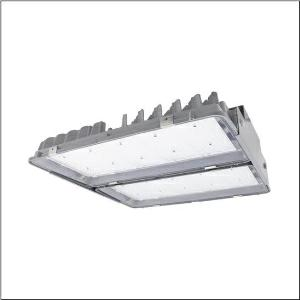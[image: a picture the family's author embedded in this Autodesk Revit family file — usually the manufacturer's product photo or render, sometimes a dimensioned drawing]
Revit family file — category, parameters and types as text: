
# Revit family: highbay_11xtreme_51hf81db4vma
name_source: partatom
category: Lighting Fixtures
units: mm (PartAtom-declared; Revit-internal decimal feet)

## family parameters
Cut with Voids When Loaded = No
Host = Face
Light Source = No
Part Type = Normal
Room Calculation Point = No
Round Connector Dimension = Use Diameter
Shared = No

## types (1)
- --- (1 x LED, 69400 lm, 380.2 W, 4000K)
    Apparent Load = 380 VA
    CIE Flux Codes = 88 96 99 100 100
    Color Rendering = 80
    Color Temperature = 4000K
    Default Elevation = 1800 mm
    Description = Highbay 11Xtreme, LED high bay luminaire, primary light control with lens, of PMMA, primary optical cover: cover, of toughened safety glass, light emission: direct distribution, primary light characteristic: symmetric, installation type: suspended mounting, surface-mounted, 2x LED module,for 1x 2x LED, rated luminous flux: 69.400lm, luminous efficacy: 183lm/W, light colour: 840, colour temperature: 4000K, with cable H07RN-F 5x 1.5mm², mains connection: 220..240V, AC, 50/60Hz, cable length: 1,5m, rated input power: 380W, luminaire housing, of diecast aluminium, partly coated, silver, length: 595mm, width: 560mm, height: 195mm, protection rating (complete): IP66, insulation class (complete): insulation class I (protective earthing), certification: CE, ENEC, UKCA, protection symbol: D, ball protection: ball impact resistant according to DIN VDE 0710 part 13 (with chain suspension), impact resistance: IK08, permissible operating ambient temperature: -25..+45°C, reducing of maximum allowable ambient temperature of 5°C with ceiling mounting, packaging unit: 1 piece
    Height = 157 mm
    Lamp = 1 x LED
    Lamp Light Flux = 69400 lm
    Lamp Power = 380.2 W
    Lamp count = 1
    Length = 593 mm
    Luminous efficacy = 183 lm/W
    Manufacturer = Siteco
    ModVariant = No
    Model = 51HF81DB4VMA
    Mounting Place = Ceiling
    Mounting Type = Pendant
    Number of Poles = 1
    OnlyDefault = Yes
    Power Factor = 1
    Product Name = Highbay 11Xtreme
    Product group = LED high bay luminaire
    ProductGroupID = 903
    Protection Class = Protection class I
    Protection Degree = IP 66
    RLX_Detail_Level = 1
    RLX_Emergency_Light_Flux = 0 lm
    RLX_Emergency_Type = 0
    RLX_Emergency_Type_DB = No
    RlxData = <blob elided: 33801 chars, md5=1dd7c901>
    Socket = socket
    Standby Power = 0 W
    System Light Flux = 69402 lm
    System Power = 380 W
    Type Comments = factory setting: luminous flux: 100 % | dim-lin: 254 | 1257 mA
    Type Image = l_1258340.jpg
    URL = http://relux.com
    VarID = @adj_045759
    Voltage = 0 V
    Weight = 0.00 kg
    Width = 568 mm

## geometry (parser evidence)
native form markers: Blend x4, Sweep x11
no freeform markers — native parametric forms only
